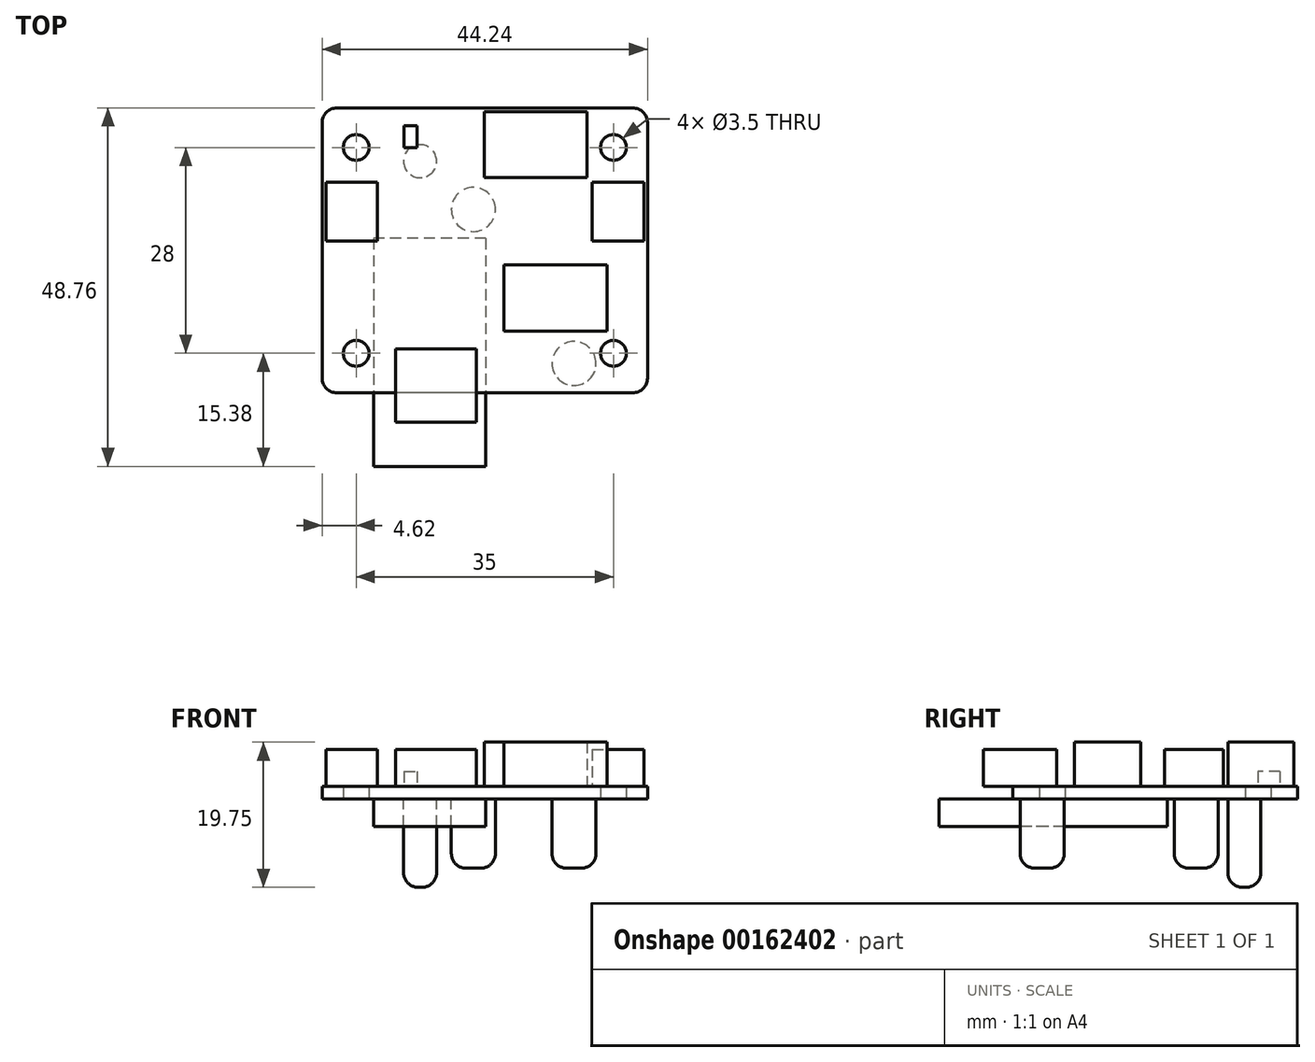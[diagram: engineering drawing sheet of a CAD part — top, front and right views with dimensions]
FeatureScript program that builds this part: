
annotation { "Feature Type Name" : "Feature", "Feature Type Description" : "" }
export const myFeature = defineFeature(function(context is Context, id is Id, definition is map)
    precondition{}
    {
        {
            var Q0;
            Q0=qCreatedBy(makeId("Top.planeOp"),FACE);
            var sketch = newSketch(context, id + "F0", { "sketchPlane" : qUnion([Q0])});
            skLineSegment(sketch, "E0.bottom", {"start": v(22.12, 19.38) * mm, "end": v(-22.12, 19.37) * mm});
            skLineSegment(sketch, "E0.top", {"start": v(22.12, -19.38) * mm, "end": v(-22.12, -19.38) * mm});
            skLineSegment(sketch, "E0.left", {"start": v(22.12, 19.38) * mm, "end": v(22.12, -19.38) * mm});
            skLineSegment(sketch, "E0.right", {"start": v(-22.12, 19.38) * mm, "end": v(-22.12, -19.38) * mm});
            skPoint(sketch, "E0.middle", {"position": v(0, 0) * mm});
            skLineSegment(sketch, "E1.bottom", {"start": v(17.5, 14) * mm, "end": v(-17.5, 14) * mm, "construction": true});
            skLineSegment(sketch, "E1.top", {"start": v(17.5, -14) * mm, "end": v(-17.5, -14) * mm, "construction": true});
            skLineSegment(sketch, "E1.left", {"start": v(17.5, 14) * mm, "end": v(17.5, -14) * mm, "construction": true});
            skLineSegment(sketch, "E1.right", {"start": v(-17.5, 14) * mm, "end": v(-17.5, -14) * mm, "construction": true});
            skCircle(sketch, "E2", {"center": v(-17.5, 14) * mm, "radius": 1.75 * mm});
            skCircle(sketch, "E3", {"center": v(-17.5, -14) * mm, "radius": 1.75 * mm});
            skCircle(sketch, "E4", {"center": v(17.5, -14) * mm, "radius": 1.75 * mm});
            skCircle(sketch, "E5", {"center": v(17.5, 14) * mm, "radius": 1.75 * mm});
            skSolve(sketch);
        }
        {
            var Q0;
            Q0=makeQuery(id+"F0.imprint","IMPRINT",FACE,{"disambiguationData":[TD([[makeQuery(id+"F0.imprint","IMPRINT",EDGE,{"derivedFrom":sQuery(id+"F0.wireOp",EDGE,"E0.bottom")}),1.0]])]});
            extrude(context, id + "F1", {"entities" : qUnion([Q0]), "depth" : 1.75 * mm});
        }
        {
            var Q0;
            Q0=makeQuery(id+"F1.opExtrude","SWEPT_EDGE",EDGE,{"disambiguationData":[OSD([sQuery(id+"F0.wireOp",EDGE,"E0.top"),sQuery(id+"F0.wireOp",EDGE,"E0.left")])]});
            var Q1;
            Q1=makeQuery(id+"F1.opExtrude","SWEPT_EDGE",EDGE,{"disambiguationData":[OSD([sQuery(id+"F0.wireOp",EDGE,"E0.top"),sQuery(id+"F0.wireOp",EDGE,"E0.right")])]});
            var Q2;
            Q2=makeQuery(id+"F1.opExtrude","SWEPT_EDGE",EDGE,{"disambiguationData":[OSD([sQuery(id+"F0.wireOp",EDGE,"E0.bottom"),sQuery(id+"F0.wireOp",EDGE,"E0.right")])]});
            var Q3;
            Q3=makeQuery(id+"F1.opExtrude","SWEPT_EDGE",EDGE,{"disambiguationData":[OSD([sQuery(id+"F0.wireOp",EDGE,"E0.bottom"),sQuery(id+"F0.wireOp",EDGE,"E0.left")])]});
            fillet(context, id + "F2", {"entities" : qUnion([Q0, Q1, Q2, Q3]), "radius" : 2 * mm, "tangentPropagation" : true, "allowEdgeOverflow" : false});
        }
        {
            var Q0;
            Q0=makeQuery(id+"F1.opExtrude","CAP_FACE",FACE,{"disambiguationData":[OSD([sQuery(id+"F0.wireOp",EDGE,"E0.bottom"),sQuery(id+"F0.wireOp",EDGE,"E0.top"),sQuery(id+"F0.wireOp",EDGE,"E0.left"),sQuery(id+"F0.wireOp",EDGE,"E0.right"),sQuery(id+"F0.wireOp",EDGE,"E2"),sQuery(id+"F0.wireOp",EDGE,"E3"),sQuery(id+"F0.wireOp",EDGE,"E4"),sQuery(id+"F0.wireOp",EDGE,"E5")])],"isStart":false});
            var sketch = newSketch(context, id + "F3", { "sketchPlane" : qUnion([Q0])});
            skLineSegment(sketch, "E6.bottom", {"start": v(-0.1, 18.88) * mm, "end": v(13.9, 18.88) * mm});
            skLineSegment(sketch, "E6.top", {"start": v(-0.1, 9.88) * mm, "end": v(13.9, 9.88) * mm});
            skLineSegment(sketch, "E6.left", {"start": v(-0.1, 18.88) * mm, "end": v(-0.1, 9.88) * mm});
            skLineSegment(sketch, "E6.right", {"start": v(13.9, 18.88) * mm, "end": v(13.9, 9.88) * mm});
            skLineSegment(sketch, "E7.bottom", {"start": v(14.62, 9.25) * mm, "end": v(21.62, 9.25) * mm});
            skLineSegment(sketch, "E7.top", {"start": v(14.62, 1.25) * mm, "end": v(21.62, 1.25) * mm});
            skLineSegment(sketch, "E7.left", {"start": v(14.62, 9.25) * mm, "end": v(14.62, 1.25) * mm});
            skLineSegment(sketch, "E7.right", {"start": v(21.62, 9.25) * mm, "end": v(21.62, 1.25) * mm});
            skLineSegment(sketch, "E8.bottom", {"start": v(2.62, -1.97) * mm, "end": v(16.62, -1.97) * mm});
            skLineSegment(sketch, "E8.top", {"start": v(2.63, -10.97) * mm, "end": v(16.62, -10.97) * mm});
            skLineSegment(sketch, "E8.left", {"start": v(2.62, -1.97) * mm, "end": v(2.63, -10.97) * mm});
            skLineSegment(sketch, "E8.right", {"start": v(16.62, -1.97) * mm, "end": v(16.62, -10.97) * mm});
            skLineSegment(sketch, "E9.bottom", {"start": v(-14.62, 9.25) * mm, "end": v(-21.62, 9.25) * mm});
            skLineSegment(sketch, "E9.top", {"start": v(-14.62, 1.25) * mm, "end": v(-21.62, 1.25) * mm});
            skLineSegment(sketch, "E9.left", {"start": v(-14.62, 9.25) * mm, "end": v(-14.62, 1.25) * mm});
            skLineSegment(sketch, "E9.right", {"start": v(-21.62, 9.25) * mm, "end": v(-21.62, 1.25) * mm});
            skLineSegment(sketch, "E10.bottom", {"start": v(-12.12, -13.38) * mm, "end": v(-1.13, -13.38) * mm});
            skLineSegment(sketch, "E10.top", {"start": v(-12.12, -23.38) * mm, "end": v(-1.12, -23.38) * mm});
            skLineSegment(sketch, "E10.left", {"start": v(-12.12, -13.38) * mm, "end": v(-12.12, -23.38) * mm});
            skLineSegment(sketch, "E10.right", {"start": v(-1.12, -13.38) * mm, "end": v(-1.12, -23.38) * mm});
            skLineSegment(sketch, "E11.bottom", {"start": v(-11, 16.97) * mm, "end": v(-9.25, 16.97) * mm});
            skLineSegment(sketch, "E11.top", {"start": v(-11, 13.97) * mm, "end": v(-9.25, 13.97) * mm});
            skLineSegment(sketch, "E11.left", {"start": v(-11, 16.97) * mm, "end": v(-11, 13.97) * mm});
            skLineSegment(sketch, "E11.right", {"start": v(-9.25, 16.97) * mm, "end": v(-9.25, 13.97) * mm});
            skSolve(sketch);
        }
        {
            var Q0;
            Q0=makeQuery(id+"F3.imprint","IMPRINT",FACE,{"disambiguationData":[TD([[makeQuery(id+"F3.imprint","IMPRINT",EDGE,{"derivedFrom":sQuery(id+"F3.wireOp",EDGE,"E6.bottom")}),-1.0]])]});
            var Q1;
            Q1=makeQuery(id+"F3.imprint","IMPRINT",FACE,{"disambiguationData":[TD([[makeQuery(id+"F3.imprint","IMPRINT",EDGE,{"derivedFrom":sQuery(id+"F3.wireOp",EDGE,"E8.bottom")}),-1.0]])]});
            extrude(context, id + "F4", {"entities" : qUnion([Q0, Q1]), "operationType" : NewBodyOperationType.ADD, "depth" : 6 * mm});
        }
        {
            var Q0;
            Q0=makeQuery(id+"F3.imprint","IMPRINT",FACE,{"disambiguationData":[TD([[makeQuery(id+"F3.imprint","IMPRINT",EDGE,{"derivedFrom":sQuery(id+"F3.wireOp",EDGE,"E9.bottom")}),1.0]])]});
            var Q1;
            Q1=makeQuery(id+"F3.imprint","IMPRINT",FACE,{"disambiguationData":[TD([[makeQuery(id+"F3.imprint","IMPRINT",EDGE,{"derivedFrom":sQuery(id+"F3.wireOp",EDGE,"E7.bottom")}),-1.0]])]});
            extrude(context, id + "F5", {"entities" : qUnion([Q0, Q1]), "operationType" : NewBodyOperationType.ADD, "depth" : 5 * mm});
        }
        {
            var Q0;
            Q0=makeQuery(id+"F3.imprint","IMPRINT",FACE,{"disambiguationData":[TD([[makeQuery(id+"F3.imprint","IMPRINT",EDGE,{"derivedFrom":sQuery(id+"F3.wireOp",EDGE,"E11.bottom")}),-1.0]])]});
            extrude(context, id + "F6", {"entities" : qUnion([Q0]), "operationType" : NewBodyOperationType.ADD, "depth" : 2 * mm});
        }
        {
            var Q0;
            {var subQ0=sQuery(id+"F3.wireOp",EDGE,"E10.bottom");Q0=makeQuery(id+"F3.imprint","IMPRINT",FACE,{"disambiguationData":[TD([[makeQuery(id+"F3.imprint","IMPRINT",EDGE,{"derivedFrom":subQ0}),-1.0]])]});}
            var Q1;
            {var subQ0=sQuery(id+"F3.wireOp",EDGE,"E10.top");Q1=makeQuery(id+"F3.imprint","IMPRINT",FACE,{"disambiguationData":[TD([[makeQuery(id+"F3.imprint","IMPRINT",EDGE,{"derivedFrom":subQ0}),1.0]])]});}
            extrude(context, id + "F7", {"entities" : qUnion([Q0, Q1]), "operationType" : NewBodyOperationType.ADD, "depth" : 5 * mm});
        }
        {
            var Q0;
            Q0=makeQuery(id+"F1.opExtrude","CAP_FACE",FACE,{"disambiguationData":[OSD([sQuery(id+"F0.wireOp",EDGE,"E0.bottom"),sQuery(id+"F0.wireOp",EDGE,"E0.top"),sQuery(id+"F0.wireOp",EDGE,"E0.left"),sQuery(id+"F0.wireOp",EDGE,"E0.right"),sQuery(id+"F0.wireOp",EDGE,"E2"),sQuery(id+"F0.wireOp",EDGE,"E3"),sQuery(id+"F0.wireOp",EDGE,"E4"),sQuery(id+"F0.wireOp",EDGE,"E5")])],"isStart":true});
            var sketch = newSketch(context, id + "F8", { "sketchPlane" : qUnion([Q0])});
            skCircle(sketch, "E12", {"center": v(-8.8, -12.12) * mm, "radius": 2.25 * mm});
            skCircle(sketch, "E13", {"center": v(-1.55, -5.57) * mm, "radius": 3 * mm});
            skCircle(sketch, "E14", {"center": v(12.12, 15.38) * mm, "radius": 3 * mm});
            skLineSegment(sketch, "E15.bottom", {"start": v(0.13, -1.62) * mm, "end": v(-15.12, -1.63) * mm});
            skLineSegment(sketch, "E15.top", {"start": v(0.12, 29.38) * mm, "end": v(-15.12, 29.38) * mm});
            skLineSegment(sketch, "E15.left", {"start": v(0.12, -1.63) * mm, "end": v(0.13, 29.38) * mm});
            skLineSegment(sketch, "E15.right", {"start": v(-15.13, -1.63) * mm, "end": v(-15.12, 29.38) * mm});
            skSolve(sketch);
        }
        {
            var Q0;
            Q0=makeQuery(id+"F8.imprint","IMPRINT",FACE,{"disambiguationData":[TD([[makeQuery(id+"F8.imprint","IMPRINT",EDGE,{"derivedFrom":sQuery(id+"F8.wireOp",EDGE,"E13")}),1.0]])]});
            var Q1;
            Q1=makeQuery(id+"F8.imprint","IMPRINT",FACE,{"disambiguationData":[TD([[makeQuery(id+"F8.imprint","IMPRINT",EDGE,{"derivedFrom":sQuery(id+"F8.wireOp",EDGE,"E14")}),1.0]])]});
            extrude(context, id + "F9", {"entities" : qUnion([Q0, Q1]), "operationType" : NewBodyOperationType.ADD, "depth" : 9.4 * mm});
        }
        {
            var Q0;
            Q0=makeQuery(id+"F8.imprint","IMPRINT",FACE,{"disambiguationData":[TD([[makeQuery(id+"F8.imprint","IMPRINT",EDGE,{"derivedFrom":sQuery(id+"F8.wireOp",EDGE,"E12")}),1.0]])]});
            extrude(context, id + "F10", {"entities" : qUnion([Q0]), "operationType" : NewBodyOperationType.ADD, "depth" : 12 * mm});
        }
        {
            var Q0;
            {var subQ0=sQuery(id+"F8.wireOp",EDGE,"E15.bottom");Q0=makeQuery(id+"F8.imprint","IMPRINT",FACE,{"disambiguationData":[TD([[makeQuery(id+"F8.imprint","IMPRINT",EDGE,{"derivedFrom":subQ0}),-1.0]])]});}
            var Q1;
            {var subQ0=sQuery(id+"F8.wireOp",EDGE,"E15.top");Q1=makeQuery(id+"F8.imprint","IMPRINT",FACE,{"disambiguationData":[TD([[makeQuery(id+"F8.imprint","IMPRINT",EDGE,{"derivedFrom":subQ0}),1.0]])]});}
            extrude(context, id + "F11", {"entities" : qUnion([Q0, Q1]), "operationType" : NewBodyOperationType.ADD, "depth" : 3.7 * mm});
        }
        {
            var Q0;
            Q0=makeQuery(id+"F9.opExtrude","CAP_FACE",FACE,{"disambiguationData":[OSD([sQuery(id+"F8.wireOp",EDGE,"E14")])],"isStart":false});
            var Q1;
            Q1=makeQuery(id+"F9.opExtrude","CAP_FACE",FACE,{"disambiguationData":[OSD([sQuery(id+"F8.wireOp",EDGE,"E13")])],"isStart":false});
            fillet(context, id + "F12", {"entities" : qUnion([Q0, Q1]), "radius" : 2 * mm, "tangentPropagation" : true, "allowEdgeOverflow" : false});
        }
        {
            var Q0;
            Q0=makeQuery(id+"F10.opExtrude","CAP_FACE",FACE,{"disambiguationData":[OSD([sQuery(id+"F8.wireOp",EDGE,"E12")])],"isStart":false});
            fillet(context, id + "F13", {"entities" : qUnion([Q0]), "radius" : 2 * mm, "tangentPropagation" : true, "allowEdgeOverflow" : false});
        }
    });
